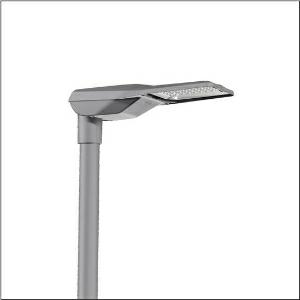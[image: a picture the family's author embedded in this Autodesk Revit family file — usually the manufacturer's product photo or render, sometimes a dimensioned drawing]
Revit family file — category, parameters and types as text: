
# Revit family: streetlight_sl_21_iq_mini___p0_8a_5xe2u31g08gb_20f9
name_source: partatom
category: Lighting Fixtures
units: mm (PartAtom-declared; Revit-internal decimal feet)

## family parameters
Cut with Voids When Loaded = No
Host = Face
Light Source = No
Part Type = Normal
Room Calculation Point = No
Round Connector Dimension = Use Diameter
Shared = No

## types (1)
- --- (1 x LED, 5730 lm, 37.1 W, 3000K)
    Apparent Load = 37 VA
    CIE Flux Codes = 33 69 96 100 100
    Color Rendering = 70
    Color Temperature = 3000K
    Default Elevation = 1800 mm
    Description = Streetlight SL 21 iQ mini, mast luminaire, primary light control with lens, of PMMA, primary optical cover: cover, of toughened safety glass, transparent, light distribution: P0.8a, light emission: direct distribution, primary light characteristic: asymmetric, installation type: post-top, side-entry, LED, High Power LED, rated luminous flux: 5.730lm, luminous efficacy: 154lm/W, light colour: 730, colour temperature: 3000K, control gear: iQ Street-Remote, control: pre-setting: linear dimming characteristic, Street-Remote, Auto-Match, Temp-Guard, Lumen-Switch, Night-Set, Smart-Wire, Light-Fading, Desk-Remote (wireless, voltage-free reading and setting of iQ features in the workshop via application-optimized NFC function/RFID function), optimised constant luminous flux control (CLO 2.0), mains connection: 220..240V, AC, 50/60Hz, start of lifetime: 37W, end of service life: 39W, reduction: 18W, luminaire housing, of diecast aluminium, powder-coated, Siteco® metallic grey (DB 702S), corrosivity category C5 mid according to DIN EN ISO 12944, please order mast flange separately, inclination adjustable: 0°, 5°, 10°, 15°, sealing non-destructively replaceable, multi-level sealing system, length: 628mm, width: 235mm, height: 110mm, mast flange for spigot size: 42mm (side-entry): 5XC10008XM4, 60/48mm (side-entry/post-top): 5XC10108XM2, 76/60mm (side-entry/post-top): 5XC10108XM1, mounting height: 4..8m, protection rating (complete): IP66, insulation class (complete): insulation class II (safety insulation), certification: CE, ENEC, ENEC+, VDE, impact resistance: IK09, permissible operating ambient temperature for outdoor applications: -40..+50°C, standard-compliant lighting for roads and squares, packaging unit: 1 piece

Light Distribution: P0.8a
    Height = 110 mm
    Lamp = 1 x LED
    Lamp Light Flux = 5730 lm
    Lamp Power = 37.1 W
    Lamp count = 1
    Length = 625 mm
    Luminous efficacy = 154 lm/W
    Manufacturer = Siteco
    ModVariant = No
    Model = 5XE2U31G08GB
    Number of Poles = 1
    OnlyDefault = Yes
    Power Factor = 1
    Product Name = Streetlight SL 21 iQ mini | P0.8a
    Product group = mast luminaire | pylon top
    ProductGroupID = 6100
    Protection Class = Protection class II
    Protection Degree = IP 66
    RLX_Detail_Level = 1
    RLX_Emergency_Light_Flux = 0 lm
    RLX_Emergency_Type = 0
    RLX_Emergency_Type_DB = No
    RlxData = <blob elided: 91837 chars, md5=3b00a5cf>
    Socket = socket
    Standby Power = 0 W
    System Light Flux = 5730 lm
    System Power = 37 W
    Type Comments = factory setting: luminous flux: 100 % | dim-lin: 254 | 385 mA
    Type Image = l_1003519.jpg
    URL = http://relux.com
    VarID = @adj_069668
    Voltage = 0 V
    Weight = 0.00 kg
    Width = 234 mm

## geometry (parser evidence)
native form markers: Blend x4, Sweep x10
no freeform markers — native parametric forms only
